# Revit family: WashbasinUnit-80cm-WithDoors-Vitra-SentoSeries-60785+60797+60809+65871
name_source: partatom
category: Furniture Systems
revit_build: Autodesk Revit 2017 (Build: 20160225_1515(x64)
units: mm (PartAtom-declared; Revit-internal decimal feet)

## family parameters
Cut with Voids When Loaded = No
Host = Face
OmniClass Number = 23.40.00.00
OmniClass Title = Equipment and Furnishings
Part Type = Normal
Room Calculation Point = No
Round Connector Dimension = Use Diameter
Shared = Yes

## types (4) — shared parameters
BIMobject category = Bathroom compound units
Brand = VitrA
Default Elevation = 580 mm
Design country = Turkey
IFC Classification = Furniture
Light Operation Type = Motion Sensor
Lighting type = Led Lighting
Main Material = Wood
Manufacturer = VitrA
Manufacturer name = VitrA
Masterformat 2014 Code = 13 42 13
Masterformat 2014 Description = Bathroom Unit Modules
Mounting type = Wall-Hung
NBS Referans Code = 35-75-08
NBS Referans Description = Bathroom Cabinets
Nominal Depth (mm) = 450 mm  [stored 1.47638 ft]
Nominal Height (mm) = 615 mm  [stored 2.01772 ft]
Nominal Width (mm) = 700 mm
OmniClass Code = 23-31 25 13
OmniClass Description = Bathroom Cabinets
Product certification = https://www.vitraglobal.com
Product family = Sento
Product group = Washbasin Unit
Product url = https://www.vitraglobal.com
Secondary Material = 178 -Natural Oak -Thermoform
Technical description = https://www.vitraglobal.com
UNSPSC Code = 301815
UNSPSC Description = Bathroom Cabinets
URL = https://vitraglobal.com
Uniclass 1.4 Code = L8241
Uniclass 1.4 Description = Bathroom Cabinets
Uniclass 2.0 Code = PR-35-75-08
Uniclass 2.0 Description = Bathroom Cabinets
Uniclass 2015 Code = Pr_40_20_93
Uniclass 2015 Name = Wash basins, sinks and troughs
Uniformat II Code = E20
Uniformat II Description = FURNISHINGS
Voltage (V) = 220V
Warranty Period (Year) = 2
Weight Net (kg) = 54
Without legs = No
Youtube = https://www.youtube.com

## per-type parameters (varying)
| type | Article No. (default) | Color | Description | Model | Primary Material | Product SKU |
| WashbasinUnit-80cm-WithDoors-Vitra-SentoSeries-60785 | 60785 | Matt White | Sento Washbasin Unit 80cm Matt White including Washbasin | 60785 | 117 -Matte White -Thermoform | 60785 |
| WashbasinUnit-80cm-WithDoors-Vitra-SentoSeries-60797 | 60797 | Matt Cream | Sento Washbasin Unit 80cm Matt Cream including Washbasin | 60797 | 250 - Matte Cream -Thermoform | 60797 |
| WashbasinUnit-80cm-WithDoors-Vitra-SentoSeries-60809 | 60809 | Matte Anthracite | Sento Washbasin Unit 80cm Matt Anthracite including Washbasin | 60809 | 251 -Matte Anthracite -Thermoform | 60809 |
| WashbasinUnit-80cm-WithDoors-Vitra-SentoSeries-65871 | 65871 | Matte Fjord Green | Sento Washbasin Unit 80cm Matte Fjord Green including Washbasin | 65871 | 319 - Matte Fjord Green - Thermoform | 65871 |

note: [stored X ft] marks values corroborated as IEEE doubles in the binary element streams (Revit-internal decimal feet)

## geometry (parser evidence)
native form markers: Sweep x4
no freeform markers — native parametric forms only
